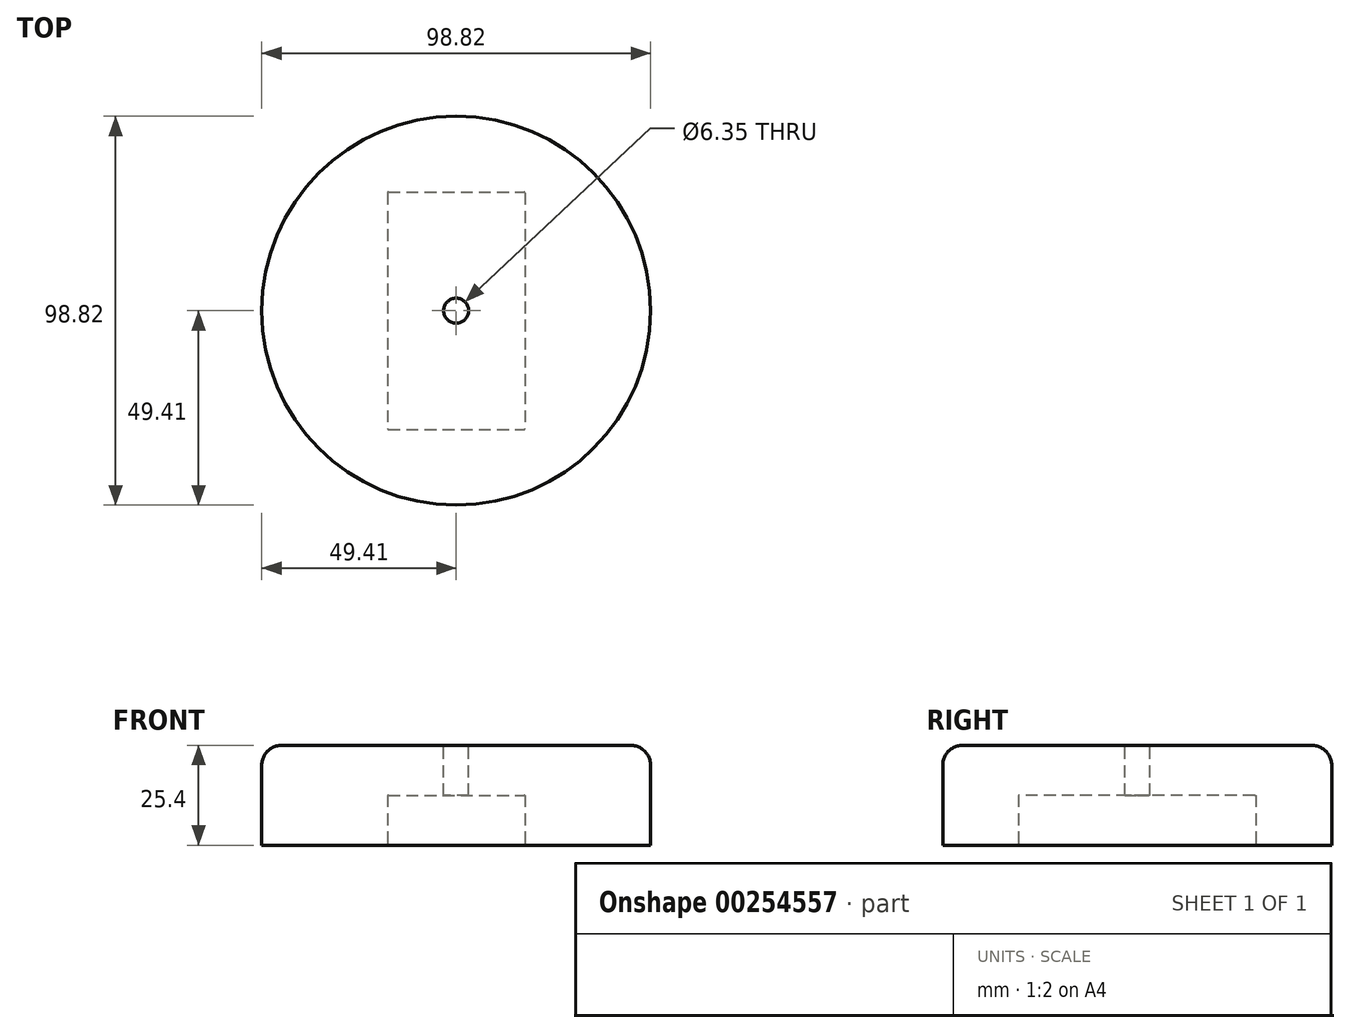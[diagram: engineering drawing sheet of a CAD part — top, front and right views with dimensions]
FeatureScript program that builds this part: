
annotation { "Feature Type Name" : "Feature", "Feature Type Description" : "" }
export const myFeature = defineFeature(function(context is Context, id is Id, definition is map)
    precondition{}
    {
        {
            var Q0;
            Q0=qCreatedBy(makeId("Top.planeOp"),FACE);
            var sketch = newSketch(context, id + "F0", { "sketchPlane" : qUnion([Q0])});
            skCircle(sketch, "E0", {"center": v(0, 0) * mm, "radius": 49.4 * mm});
            skSolve(sketch);
        }
        {
            var Q0;
            Q0=makeQuery(id+"F0.imprint","IMPRINT",FACE,{"disambiguationData":[TD([[makeQuery(id+"F0.imprint","IMPRINT",EDGE,{"derivedFrom":sQuery(id+"F0.wireOp",EDGE,"E0")}),1.0]])]});
            extrude(context, id + "F1", {"entities" : qUnion([Q0]), "depth" : 25.4 * mm});
        }
        {
            var Q0;
            Q0=makeQuery(id+"F1.opExtrude","CAP_FACE",FACE,{"disambiguationData":[OSD([sQuery(id+"F0.wireOp",EDGE,"E0")])],"isStart":false});
            var sketch = newSketch(context, id + "F2", { "sketchPlane" : qUnion([Q0])});
            skCircle(sketch, "E1", {"center": v(0, 0) * mm, "radius": 20.66 * mm});
            skSolve(sketch);
        }
        {
            var Q0;
            Q0=sQuery(id+"F2.wireOp",VERTEX,"E1.center");
            var Q1;
            Q1=makeQuery(id+"F1.opExtrude","SWEPT_BODY",BODY,{"disambiguationData":[OSD([sQuery(id+"F0.wireOp",EDGE,"E0")])]});
            hole(context, id + "F3", {"style" : HoleStyle.SIMPLE, "endStyle" : HoleEndStyle.THROUGH, "holeDiameter" : 6.35 * mm, "tappedDepth" : 12.7 * mm, "tapClearance" : 3, "locations" : qUnion([Q0]), "scope" : qUnion([Q1])});
        }
        {
            var Q0;
            Q0=makeQuery(id+"F1.opExtrude","CAP_FACE",FACE,{"disambiguationData":[OSD([sQuery(id+"F0.wireOp",EDGE,"E0")])],"isStart":true});
            var sketch = newSketch(context, id + "F4", { "sketchPlane" : qUnion([Q0])});
            skLineSegment(sketch, "E2.bottom", {"start": v(-17.46, -30.16) * mm, "end": v(17.46, -30.16) * mm});
            skLineSegment(sketch, "E2.top", {"start": v(-17.46, 30.16) * mm, "end": v(17.46, 30.16) * mm});
            skLineSegment(sketch, "E2.left", {"start": v(-17.46, -30.16) * mm, "end": v(-17.46, 30.16) * mm});
            skLineSegment(sketch, "E2.right", {"start": v(17.46, -30.16) * mm, "end": v(17.46, 30.16) * mm});
            skPoint(sketch, "E2.middle", {"position": v(0, 0) * mm});
            skSolve(sketch);
        }
        {
            var Q0;
            Q0=makeQuery(id+"F4.imprint","IMPRINT",FACE,{"disambiguationData":[TD([[makeQuery(id+"F4.imprint","IMPRINT",EDGE,{"derivedFrom":sQuery(id+"F4.wireOp",EDGE,"E2.bottom")}),1.0]])]});
            extrude(context, id + "F5", {"entities" : qUnion([Q0]), "operationType" : NewBodyOperationType.REMOVE, "oppositeDirection" : true, "depth" : 12.7 * mm});
        }
        {
            var Q0;
            Q0=makeQuery(id+"F1.opExtrude","CAP_EDGE",EDGE,{"disambiguationData":[OSD([sQuery(id+"F0.wireOp",EDGE,"E0")])],"isStart":false});
            fillet(context, id + "F6", {"entities" : qUnion([Q0]), "radius" : 5.08 * mm, "tangentPropagation" : true, "allowEdgeOverflow" : false});
        }
        {
            var Q0;
            Q0=makeQuery(id+"F5.boolean.opBoolean","COPY",EDGE,{"derivedFrom":makeQuery(id+"F5.opExtrude","SWEPT_EDGE",EDGE,{"disambiguationData":[OSD([sQuery(id+"F4.wireOp",EDGE,"E2.bottom"),sQuery(id+"F4.wireOp",EDGE,"E2.left")])]})});
            var Q1;
            Q1=makeQuery(id+"F5.boolean.opBoolean","COPY",EDGE,{"derivedFrom":makeQuery(id+"F5.opExtrude","SWEPT_EDGE",EDGE,{"disambiguationData":[OSD([sQuery(id+"F4.wireOp",EDGE,"E2.bottom"),sQuery(id+"F4.wireOp",EDGE,"E2.right")])]})});
            var Q2;
            Q2=makeQuery(id+"F5.boolean.opBoolean","COPY",EDGE,{"derivedFrom":makeQuery(id+"F5.opExtrude","SWEPT_EDGE",EDGE,{"disambiguationData":[OSD([sQuery(id+"F4.wireOp",EDGE,"E2.top"),sQuery(id+"F4.wireOp",EDGE,"E2.left")])]})});
            var Q3;
            Q3=makeQuery(id+"F5.boolean.opBoolean","COPY",EDGE,{"derivedFrom":makeQuery(id+"F5.opExtrude","SWEPT_EDGE",EDGE,{"disambiguationData":[OSD([sQuery(id+"F4.wireOp",EDGE,"E2.top"),sQuery(id+"F4.wireOp",EDGE,"E2.right")])]})});
            fillet(context, id + "F7", {"entities" : qUnion([Q0, Q1, Q2, Q3]), "radius" : 0.25 * mm, "tangentPropagation" : true, "allowEdgeOverflow" : false});
        }
    });
